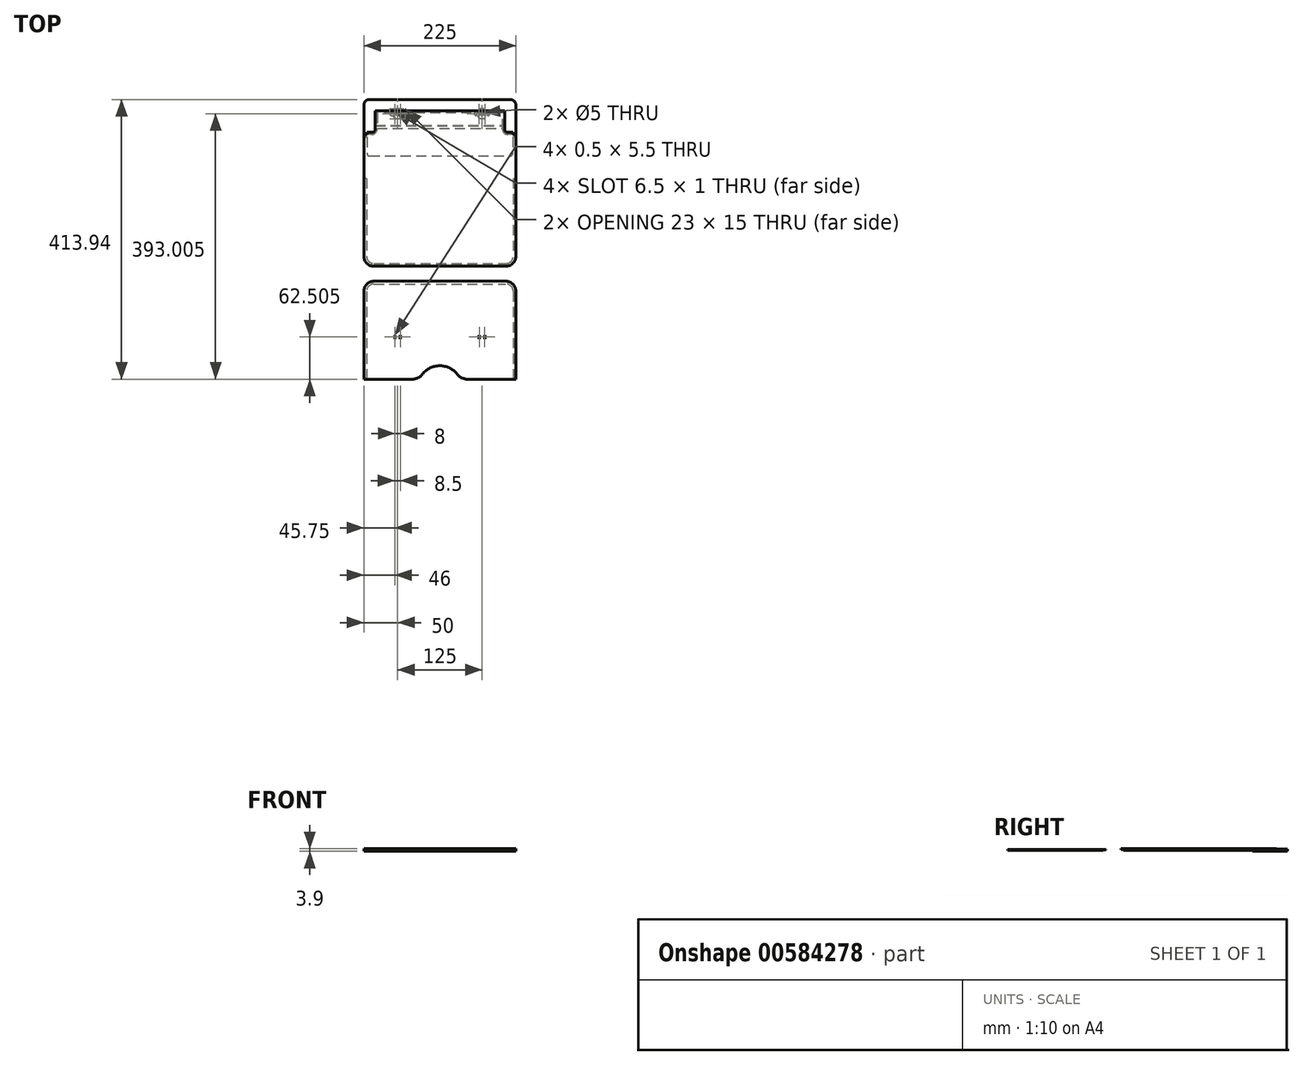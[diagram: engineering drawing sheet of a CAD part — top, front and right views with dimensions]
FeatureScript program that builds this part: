
annotation { "Feature Type Name" : "Feature", "Feature Type Description" : "" }
export const myFeature = defineFeature(function(context is Context, id is Id, definition is map)
    precondition{}
    {
        {
            var Q0;
            Q0=qCreatedBy(makeId("Top.planeOp"),FACE);
            var sketch = newSketch(context, id + "F0", { "sketchPlane" : qUnion([Q0])});
            skLineSegment(sketch, "E0.bottom", {"start": v(104.5, 206.97) * mm, "end": v(-104.5, 206.97) * mm});
            skLineSegment(sketch, "E0.top", {"start": v(-41.23, -206.97) * mm, "end": v(-112.5, -206.97) * mm});
            skLineSegment(sketch, "E0.left", {"start": v(112.5, 198.97) * mm, "end": v(112.5, 105.24) * mm});
            skLineSegment(sketch, "E0.right", {"start": v(-112.5, 198.97) * mm, "end": v(-112.5, 105.24) * mm});
            skPoint(sketch, "E0.middle", {"position": v(0, 0) * mm});
            skPoint(sketch, "E1", {"position": v(112.5, 123.54) * mm});
            skLineSegment(sketch, "E2", {"start": v(112.5, 155.4) * mm, "end": v(100.8, 155.4) * mm});
            skLineSegment(sketch, "E3", {"start": v(92.8, 163.4) * mm, "end": v(92.8, 187.27) * mm});
            skLineSegment(sketch, "E4", {"start": v(92.8, 187.27) * mm, "end": v(-92.8, 187.27) * mm});
            skLineSegment(sketch, "E5", {"start": v(-92.8, 187.27) * mm, "end": v(-92.8, 163.4) * mm});
            skLineSegment(sketch, "E6", {"start": v(-100.8, 155.4) * mm, "end": v(-112.5, 155.4) * mm});
            skLineSegment(sketch, "E7", {"start": v(-60.78, 187.27) * mm, "end": v(-60.78, 206.97) * mm, "construction": true});
            skPoint(sketch, "E8.visualSharp", {"position": v(-112.5, 206.97) * mm});
            skArc(sketch, "E8.filletArc", {"start": v(-104.5, 206.97) * mm, "mid": v(-110.16, 204.62) * mm, "end": v(-112.5, 198.97) * mm});
            skPoint(sketch, "E9.visualSharp", {"position": v(112.5, 206.97) * mm});
            skArc(sketch, "E9.filletArc", {"start": v(112.5, 198.97) * mm, "mid": v(110.16, 204.62) * mm, "end": v(104.5, 206.97) * mm});
            skPoint(sketch, "E10.visualSharp", {"position": v(92.8, 155.4) * mm});
            skArc(sketch, "E10.filletArc", {"start": v(92.8, 163.4) * mm, "mid": v(95.14, 157.74) * mm, "end": v(100.8, 155.4) * mm});
            skPoint(sketch, "E11.visualSharp", {"position": v(-92.8, 155.4) * mm});
            skArc(sketch, "E11.filletArc", {"start": v(-100.8, 155.4) * mm, "mid": v(-95.14, 157.74) * mm, "end": v(-92.8, 163.4) * mm});
            skLineSegment(sketch, "E12", {"start": v(-112.5, 145.44) * mm, "end": v(-92.8, 145.44) * mm, "construction": true});
            skLineSegment(sketch, "E13", {"start": v(112.5, 123.54) * mm, "end": v(-112.5, 123.54) * mm, "construction": true});
            skArc(sketch, "E14", {"start": v(25.52, -199.35) * mm, "mid": v(0, -186.97) * mm, "end": v(-25.52, -199.35) * mm});
            skPoint(sketch, "E15.newPointA", {"position": v(-30, -206.97) * mm});
            skPoint(sketch, "E15.newPointB", {"position": v(112.5, -206.97) * mm});
            skArc(sketch, "E15.filletArc", {"start": v(-41.23, -206.96) * mm, "mid": v(-32.5, -204.96) * mm, "end": v(-25.52, -199.35) * mm});
            skLineSegment(sketch, "E16", {"start": v(41.23, -206.97) * mm, "end": v(132.5, -206.96) * mm});
            skPoint(sketch, "E17.visualSharp", {"position": v(30, -206.97) * mm});
            skArc(sketch, "E17.filletArc", {"start": v(25.52, -199.35) * mm, "mid": v(32.5, -204.96) * mm, "end": v(41.23, -206.96) * mm});
            skLineSegment(sketch, "E18.0", {"start": v(-100.8, 158.4) * mm, "end": v(-108, 158.4) * mm});
            skArc(sketch, "E18.1", {"start": v(-100.8, 158.4) * mm, "mid": v(-97.26, 159.86) * mm, "end": v(-95.8, 163.4) * mm});
            skLineSegment(sketch, "E18.2", {"start": v(-95.8, 190.27) * mm, "end": v(-95.8, 163.4) * mm});
            skLineSegment(sketch, "E18.3", {"start": v(108, 158.4) * mm, "end": v(100.8, 158.4) * mm});
            skArc(sketch, "E18.4", {"start": v(95.8, 163.4) * mm, "mid": v(97.26, 159.86) * mm, "end": v(100.8, 158.4) * mm});
            skLineSegment(sketch, "E18.5", {"start": v(95.8, 163.4) * mm, "end": v(95.8, 190.27) * mm});
            skLineSegment(sketch, "E18.6", {"start": v(95.8, 190.27) * mm, "end": v(-95.8, 190.27) * mm});
            skLineSegment(sketch, "E19", {"start": v(-108, 158.4) * mm, "end": v(-108, 155.4) * mm});
            skLineSegment(sketch, "E20.MirrorCS", {"start": v(108, 158.4) * mm, "end": v(108, 155.4) * mm});
            skLineSegment(sketch, "E21", {"start": v(-97.5, -61.97) * mm, "end": v(97.5, -61.97) * mm});
            skLineSegment(sketch, "E22", {"start": v(-97.5, -39.77) * mm, "end": v(97.5, -39.77) * mm});
            skArc(sketch, "E23.filletArc", {"start": v(-112.5, -24.77) * mm, "mid": v(-108.1, -35.37) * mm, "end": v(-97.5, -39.77) * mm});
            skArc(sketch, "E24.filletArc", {"start": v(97.5, -39.77) * mm, "mid": v(108.1, -35.37) * mm, "end": v(112.5, -24.77) * mm});
            skLineSegment(sketch, "E25", {"start": v(-112.5, -76.97) * mm, "end": v(-112.5, -206.97) * mm});
            skLineSegment(sketch, "E26", {"start": v(112.5, -76.96) * mm, "end": v(112.5, -206.97) * mm});
            skPoint(sketch, "E27.visualSharp", {"position": v(-112.5, -61.97) * mm});
            skArc(sketch, "E27.filletArc", {"start": v(-97.5, -61.97) * mm, "mid": v(-108.1, -66.36) * mm, "end": v(-112.5, -76.97) * mm});
            skPoint(sketch, "E28.visualSharp", {"position": v(112.5, -61.97) * mm});
            skArc(sketch, "E28.filletArc", {"start": v(112.5, -76.96) * mm, "mid": v(108.1, -66.36) * mm, "end": v(97.5, -61.97) * mm});
            skLineSegment(sketch, "E29.bottom", {"start": v(-66.75, -141.72) * mm, "end": v(-66.25, -141.72) * mm});
            skLineSegment(sketch, "E29.top", {"start": v(-66.75, -147.22) * mm, "end": v(-66.25, -147.22) * mm});
            skLineSegment(sketch, "E29.left", {"start": v(-66.75, -141.72) * mm, "end": v(-66.75, -147.22) * mm});
            skLineSegment(sketch, "E29.right", {"start": v(-66.25, -141.72) * mm, "end": v(-66.25, -147.22) * mm});
            skLineSegment(sketch, "E30", {"start": v(-62.5, -148.65) * mm, "end": v(-62.5, -157.3) * mm, "construction": true});
            skPoint(sketch, "E31.orphan", {"position": v(-90.2, -187.28) * mm});
            skLineSegment(sketch, "E32.MirrorCS", {"start": v(-58.25, -147.22) * mm, "end": v(-58.75, -147.22) * mm});
            skLineSegment(sketch, "E33.MirrorCS", {"start": v(-58.75, -141.72) * mm, "end": v(-58.75, -147.22) * mm});
            skLineSegment(sketch, "E34.MirrorCS", {"start": v(-58.25, -141.72) * mm, "end": v(-58.25, -147.22) * mm});
            skLineSegment(sketch, "E35.MirrorCS", {"start": v(-58.25, -141.72) * mm, "end": v(-58.75, -141.72) * mm});
            skPoint(sketch, "E36", {"position": v(-62.5, -144.47) * mm});
            skLineSegment(sketch, "E37.trimOffspring", {"start": v(-66.25, -144.47) * mm, "end": v(-58.75, -144.47) * mm, "construction": true});
            skPoint(sketch, "E38.trimOffspring.end.orphan", {"position": v(-58.18, -144.47) * mm});
            skPoint(sketch, "E39.start.orphan", {"position": v(-66.82, -144.47) * mm});
            skLineSegment(sketch, "E40.MirrorCS", {"start": v(66.75, -147.22) * mm, "end": v(66.25, -147.22) * mm});
            skLineSegment(sketch, "E41.MirrorCS", {"start": v(66.75, -141.72) * mm, "end": v(66.25, -141.72) * mm});
            skLineSegment(sketch, "E42.MirrorCS", {"start": v(58.25, -141.72) * mm, "end": v(58.75, -141.72) * mm});
            skLineSegment(sketch, "E43.MirrorCS", {"start": v(58.25, -147.22) * mm, "end": v(58.75, -147.22) * mm});
            skPoint(sketch, "E44.MirrorP", {"position": v(66.82, -144.47) * mm});
            skLineSegment(sketch, "E45.MirrorCS", {"start": v(58.25, -141.72) * mm, "end": v(58.25, -147.21) * mm});
            skLineSegment(sketch, "E46.MirrorCS", {"start": v(66.25, -144.47) * mm, "end": v(58.75, -144.47) * mm, "construction": true});
            skLineSegment(sketch, "E47.MirrorCS", {"start": v(66.25, -141.72) * mm, "end": v(66.25, -147.21) * mm});
            skPoint(sketch, "E48.MirrorP", {"position": v(62.5, -144.47) * mm});
            skLineSegment(sketch, "E49.MirrorCS", {"start": v(66.75, -141.72) * mm, "end": v(66.75, -147.21) * mm});
            skLineSegment(sketch, "E50.MirrorCS", {"start": v(58.75, -141.72) * mm, "end": v(58.75, -147.21) * mm});
            skPoint(sketch, "E51.MirrorP", {"position": v(58.18, -144.47) * mm});
            skLineSegment(sketch, "E52", {"start": v(-112.5, 105.24) * mm, "end": v(112.5, 105.24) * mm, "construction": true});
            skLineSegment(sketch, "E53", {"start": v(-112.5, 105.24) * mm, "end": v(-112.5, -24.77) * mm});
            skLineSegment(sketch, "E54", {"start": v(112.5, 105.24) * mm, "end": v(112.5, -24.77) * mm});
            skSolve(sketch);
        }
        {
            var Q0;
            {var subQ1=sQuery(id+"F0.wireOp",EDGE,"E0.top");Q0=makeQuery(id+"F0.imprint","IMPRINT",FACE,{"disambiguationData":[TD([[makeQuery(id+"F0.imprint","IMPRINT",EDGE,{"derivedFrom":subQ1}),-1.0]])]});}
            extrude(context, id + "F1", {"entities" : qUnion([Q0]), "oppositeDirection" : true, "depth" : 0.8 * mm, "offsetDistance" : 25 * mm});
        }
        {
            var Q0;
            Q0=makeQuery(id+"F0.imprint","IMPRINT",FACE,{"disambiguationData":[TD([[makeQuery(id+"F0.imprint","IMPRINT",EDGE,{"derivedFrom":sQuery(id+"F0.wireOp",EDGE,"E3")}),1.0]])]});
            var Q1;
            Q1=makeQuery(id+"F0.imprint","IMPRINT",FACE,{"disambiguationData":[TD([[makeQuery(id+"F0.imprint","IMPRINT",EDGE,{"derivedFrom":sQuery(id+"F0.wireOp",EDGE,"E3")}),-1.0]])]});
            extrude(context, id + "F2", {"entities" : qUnion([Q0, Q1]), "depth" : 0.9 * mm, "offsetDistance" : 25 * mm});
        }
        {
            var Q0;
            Q0=makeQuery(id+"F0.imprint","IMPRINT",FACE,{"disambiguationData":[TD([[makeQuery(id+"F0.imprint","IMPRINT",EDGE,{"derivedFrom":sQuery(id+"F0.wireOp",EDGE,"E0.bottom")}),1.0]])]});
            extrude(context, id + "F3", {"entities" : qUnion([Q0]), "oppositeDirection" : true, "depth" : 0.9 * mm, "offsetDistance" : 25 * mm});
        }
        {
            var Q0;
            Q0=makeQuery(id+"F0.imprint","IMPRINT",FACE,{"disambiguationData":[TD([[makeQuery(id+"F0.imprint","IMPRINT",EDGE,{"derivedFrom":sQuery(id+"F0.wireOp",EDGE,"E3")}),-1.0]])]});
            var Q1;
            Q1=makeQuery(id+"F0.imprint","IMPRINT",FACE,{"disambiguationData":[TD([[makeQuery(id+"F0.imprint","IMPRINT",EDGE,{"derivedFrom":sQuery(id+"F0.wireOp",EDGE,"E0.bottom")}),1.0]])]});
            extrude(context, id + "F4", {"entities" : qUnion([Q0, Q1]), "depth" : 0.6 * mm, "offsetDistance" : 25 * mm});
        }
        {
            var Q0;
            Q0=makeQuery(id+"F3.opExtrude","CAP_FACE",FACE,{"disambiguationData":[OSD([sQuery(id+"F0.wireOp",EDGE,"E0.bottom"),sQuery(id+"F0.wireOp",EDGE,"E0.left"),sQuery(id+"F0.wireOp",EDGE,"E0.right"),sQuery(id+"F0.wireOp",EDGE,"E2"),sQuery(id+"F0.wireOp",EDGE,"E6"),sQuery(id+"F0.wireOp",EDGE,"E8.filletArc"),sQuery(id+"F0.wireOp",EDGE,"E9.filletArc"),sQuery(id+"F0.wireOp",EDGE,"E18.0"),sQuery(id+"F0.wireOp",EDGE,"E18.2"),sQuery(id+"F0.wireOp",EDGE,"E18.3"),sQuery(id+"F0.wireOp",EDGE,"E18.5"),sQuery(id+"F0.wireOp",EDGE,"E18.6"),sQuery(id+"F0.wireOp",EDGE,"E19"),sQuery(id+"F0.wireOp",EDGE,"E20.MirrorCS")])],"isStart":false});
            var sketch = newSketch(context, id + "F5", { "sketchPlane" : qUnion([Q0])});
            skLineSegment(sketch, "E55.0", {"start": v(-112.5, -198.97) * mm, "end": v(-112.5, -155.4) * mm});
            skArc(sketch, "E56.0", {"start": v(-104.5, -206.97) * mm, "mid": v(-110.16, -204.62) * mm, "end": v(-112.5, -198.97) * mm});
            skLineSegment(sketch, "E57.0", {"start": v(104.5, -206.97) * mm, "end": v(-104.5, -206.97) * mm});
            skArc(sketch, "E58.0", {"start": v(112.5, -198.97) * mm, "mid": v(110.16, -204.62) * mm, "end": v(104.5, -206.97) * mm});
            skLineSegment(sketch, "E59.0", {"start": v(112.5, -198.97) * mm, "end": v(112.5, -155.4) * mm});
            skPoint(sketch, "E60.orphan", {"position": v(-112.5, -105.24) * mm});
            skPoint(sketch, "E61.orphan", {"position": v(112.5, -105.24) * mm});
            skLineSegment(sketch, "E62", {"start": v(-108, -151.26) * mm, "end": v(-108, -127.54) * mm});
            skArc(sketch, "E63", {"start": v(-108.36, -151.66) * mm, "mid": v(-110.78, -152.87) * mm, "end": v(-111.75, -155.4) * mm});
            skArc(sketch, "E64.filletArc", {"start": v(-108.36, -151.66) * mm, "mid": v(-108.1, -151.53) * mm, "end": v(-108, -151.26) * mm});
            skLineSegment(sketch, "E65.0", {"start": v(0, -123.54) * mm, "end": v(-104, -123.54) * mm});
            skPoint(sketch, "E66.newPointB", {"position": v(-112.5, -123.54) * mm});
            skArc(sketch, "E66.filletArc", {"start": v(-104, -123.54) * mm, "mid": v(-106.83, -124.7) * mm, "end": v(-108, -127.54) * mm});
            skPoint(sketch, "E67.orphan", {"position": v(112.5, -123.54) * mm});
            skLineSegment(sketch, "E68.MirrorCS", {"start": v(0, -123.54) * mm, "end": v(104, -123.54) * mm});
            skArc(sketch, "E69.MirrorCS", {"start": v(104, -123.54) * mm, "mid": v(106.83, -124.7) * mm, "end": v(108, -127.54) * mm});
            skLineSegment(sketch, "E70.MirrorCS", {"start": v(108, -151.26) * mm, "end": v(108, -127.54) * mm});
            skArc(sketch, "E71.MirrorCS", {"start": v(108.36, -151.66) * mm, "mid": v(108.1, -151.53) * mm, "end": v(108, -151.26) * mm});
            skArc(sketch, "E72.MirrorCS", {"start": v(108.36, -151.66) * mm, "mid": v(110.78, -152.87) * mm, "end": v(111.75, -155.4) * mm});
            skLineSegment(sketch, "E73", {"start": v(-112.5, -155.4) * mm, "end": v(-111.75, -155.4) * mm});
            skLineSegment(sketch, "E74", {"start": v(111.75, -155.4) * mm, "end": v(112.5, -155.4) * mm});
            skSolve(sketch);
        }
        {
            var Q0;
            Q0=qSketchRegion(id+"F5",true);
            extrude(context, id + "F6", {"entities" : qUnion([Q0]), "depth" : 0.6 * mm, "offsetDistance" : 25 * mm});
        }
        {
            var Q0;
            Q0=makeQuery(id+"F6.opExtrude","CAP_FACE",FACE,{"disambiguationData":[OSD([sQuery(id+"F5.wireOp",EDGE,"E55.0"),sQuery(id+"F5.wireOp",EDGE,"E56.0"),sQuery(id+"F5.wireOp",EDGE,"E57.0"),sQuery(id+"F5.wireOp",EDGE,"E58.0"),sQuery(id+"F5.wireOp",EDGE,"E59.0"),sQuery(id+"F5.wireOp",EDGE,"mqd3fcgL-vkYM-jt8C-SEZb-QTAqxbzKtnkH"),sQuery(id+"F5.wireOp",EDGE,"E62"),sQuery(id+"F5.wireOp",EDGE,"E63"),sQuery(id+"F5.wireOp",EDGE,"030e1fa7-f3c1-437d-8277-750ec2e293a4.filletArc"),sQuery(id+"F5.wireOp",EDGE,"E64.filletArc"),sQuery(id+"F5.wireOp",EDGE,"E65.0"),sQuery(id+"F5.wireOp",EDGE,"E66.filletArc"),sQuery(id+"F5.wireOp",EDGE,"E68.MirrorCS"),sQuery(id+"F5.wireOp",EDGE,"E69.MirrorCS"),sQuery(id+"F5.wireOp",EDGE,"E70.MirrorCS"),sQuery(id+"F5.wireOp",EDGE,"E71.MirrorCS"),sQuery(id+"F5.wireOp",EDGE,"E72.MirrorCS"),sQuery(id+"F5.wireOp",EDGE,"eea31a7d-e614-436a-bde2-b2130c57034b0.MirrorCS"),sQuery(id+"F5.wireOp",EDGE,"bd1179cf-cb36-4206-b0af-3bf9bbb72a3d0.MirrorCS")])],"isStart":false});
            var sketch = newSketch(context, id + "F7", { "sketchPlane" : qUnion([Q0])});
            skLineSegment(sketch, "E75.0.0", {"start": v(-108, -155.4) * mm, "end": v(-108, -158.4) * mm});
            skLineSegment(sketch, "E75.0.1", {"start": v(-108, -158.4) * mm, "end": v(-100.8, -158.4) * mm});
            skArc(sketch, "E75.0.2", {"start": v(-100.8, -158.4) * mm, "mid": v(-97.26, -159.86) * mm, "end": v(-95.8, -163.4) * mm});
            skLineSegment(sketch, "E75.0.3", {"start": v(-95.8, -163.4) * mm, "end": v(-95.8, -168.4) * mm});
            skLineSegment(sketch, "E75.0.5", {"start": v(95.8, -168.4) * mm, "end": v(95.8, -163.4) * mm});
            skArc(sketch, "E75.0.6", {"start": v(95.8, -163.4) * mm, "mid": v(97.26, -159.86) * mm, "end": v(100.8, -158.4) * mm});
            skLineSegment(sketch, "E75.0.7", {"start": v(100.8, -158.4) * mm, "end": v(108, -158.4) * mm});
            skLineSegment(sketch, "E75.0.8", {"start": v(108, -158.4) * mm, "end": v(108, -155.4) * mm});
            skLineSegment(sketch, "E75.0.9", {"start": v(108, -155.4) * mm, "end": v(112.5, -155.4) * mm});
            skLineSegment(sketch, "E75.0.10", {"start": v(112.5, -155.4) * mm, "end": v(112.5, -198.97) * mm});
            skArc(sketch, "E75.0.11", {"start": v(112.5, -198.97) * mm, "mid": v(110.16, -204.62) * mm, "end": v(104.5, -206.96) * mm});
            skLineSegment(sketch, "E75.0.12", {"start": v(104.5, -206.97) * mm, "end": v(-104.5, -206.97) * mm});
            skArc(sketch, "E75.0.13", {"start": v(-104.5, -206.97) * mm, "mid": v(-110.16, -204.62) * mm, "end": v(-112.5, -198.97) * mm});
            skLineSegment(sketch, "E75.0.14", {"start": v(-112.5, -198.97) * mm, "end": v(-112.5, -155.4) * mm});
            skLineSegment(sketch, "E75.0.15", {"start": v(-112.5, -155.4) * mm, "end": v(-108, -155.4) * mm});
            skLineSegment(sketch, "E76", {"start": v(-95.8, -168.4) * mm, "end": v(95.8, -168.4) * mm});
            skPoint(sketch, "E75.0.4.end.orphan", {"position": v(95.8, -190.27) * mm});
            skPoint(sketch, "E75.0.4.start.orphan", {"position": v(-95.8, -190.27) * mm});
            skArc(sketch, "E77", {"start": v(-69.57, -188.54) * mm, "mid": v(-62.5, -193.54) * mm, "end": v(-55.43, -188.54) * mm});
            skLineSegment(sketch, "E78", {"start": v(-71.5, -186.04) * mm, "end": v(-53.5, -186.04) * mm, "construction": true});
            skLineSegment(sketch, "E79", {"start": v(-62.5, -233.39) * mm, "end": v(-62.5, -178.54) * mm, "construction": true});
            skArc(sketch, "E80.0.startCap", {"start": v(-71.5, -188.54) * mm, "mid": v(-74, -186.04) * mm, "end": v(-71.5, -183.54) * mm});
            skArc(sketch, "E80.0.endCap", {"start": v(-53.5, -183.54) * mm, "mid": v(-51, -186.04) * mm, "end": v(-53.5, -188.54) * mm});
            skLineSegment(sketch, "E80.0.left", {"start": v(-71.5, -183.54) * mm, "end": v(-69.57, -183.54) * mm});
            skLineSegment(sketch, "E80.0.right", {"start": v(-71.5, -188.54) * mm, "end": v(-69.57, -188.54) * mm});
            skLineSegment(sketch, "E81.trimOffspring", {"start": v(-55.43, -183.54) * mm, "end": v(-53.5, -183.54) * mm});
            skLineSegment(sketch, "E82.trimOffspring", {"start": v(-55.43, -188.54) * mm, "end": v(-53.5, -188.54) * mm});
            skArc(sketch, "E83.trimOffspring", {"start": v(-55.43, -183.53) * mm, "mid": v(-62.5, -178.54) * mm, "end": v(-69.57, -183.53) * mm});
            skArc(sketch, "E84.MirrorCS", {"start": v(69.57, -188.54) * mm, "mid": v(62.5, -193.54) * mm, "end": v(55.43, -188.54) * mm});
            skLineSegment(sketch, "E85.MirrorCS", {"start": v(71.5, -188.54) * mm, "end": v(69.57, -188.54) * mm});
            skArc(sketch, "E86.MirrorCS", {"start": v(71.5, -188.54) * mm, "mid": v(74, -186.04) * mm, "end": v(71.5, -183.54) * mm});
            skLineSegment(sketch, "E87.MirrorCS", {"start": v(71.5, -183.54) * mm, "end": v(69.57, -183.54) * mm});
            skArc(sketch, "E88.MirrorCS", {"start": v(55.43, -183.53) * mm, "mid": v(62.5, -178.54) * mm, "end": v(69.57, -183.53) * mm});
            skLineSegment(sketch, "E89.MirrorCS", {"start": v(55.43, -183.54) * mm, "end": v(53.5, -183.54) * mm});
            skArc(sketch, "E90.MirrorCS", {"start": v(53.5, -183.54) * mm, "mid": v(51, -186.04) * mm, "end": v(53.5, -188.54) * mm});
            skLineSegment(sketch, "E91.MirrorCS", {"start": v(55.43, -188.54) * mm, "end": v(53.5, -188.54) * mm});
            skSolve(sketch);
        }
        {
            var Q0;
            {var subQ1=sQuery(id+"F7.wireOp",EDGE,"E75.0.0");Q0=makeQuery(id+"F7.imprint","IMPRINT",FACE,{"disambiguationData":[TD([[makeQuery(id+"F7.imprint","IMPRINT",EDGE,{"derivedFrom":subQ1}),-1.0]])]});}
            extrude(context, id + "F8", {"entities" : qUnion([Q0]), "depth" : 0.9 * mm, "offsetDistance" : 25 * mm});
        }
        {
            var Q0;
            Q0=makeQuery(id+"F8.opExtrude","CAP_FACE",FACE,{"disambiguationData":[OSD([sQuery(id+"F5.wireOp",EDGE,"mqd3fcgL-vkYM-jt8C-SEZb-QTAqxbzKtnkH"),sQuery(id+"F5.wireOp",EDGE,"030e1fa7-f3c1-437d-8277-750ec2e293a4.filletArc"),sQuery(id+"F5.wireOp",EDGE,"eea31a7d-e614-436a-bde2-b2130c57034b0.MirrorCS"),sQuery(id+"F5.wireOp",EDGE,"bd1179cf-cb36-4206-b0af-3bf9bbb72a3d0.MirrorCS"),sQuery(id+"F7.wireOp",EDGE,"E75.0.0"),sQuery(id+"F7.wireOp",EDGE,"E75.0.1"),sQuery(id+"F7.wireOp",EDGE,"E75.0.2"),sQuery(id+"F7.wireOp",EDGE,"E75.0.3"),sQuery(id+"F7.wireOp",EDGE,"E75.0.5"),sQuery(id+"F7.wireOp",EDGE,"E75.0.6"),sQuery(id+"F7.wireOp",EDGE,"E75.0.7"),sQuery(id+"F7.wireOp",EDGE,"E75.0.8"),sQuery(id+"F7.wireOp",EDGE,"E75.0.9"),sQuery(id+"F7.wireOp",EDGE,"E75.0.10"),sQuery(id+"F7.wireOp",EDGE,"E75.0.11"),sQuery(id+"F7.wireOp",EDGE,"E75.0.12"),sQuery(id+"F7.wireOp",EDGE,"E75.0.13"),sQuery(id+"F7.wireOp",EDGE,"E75.0.14"),sQuery(id+"F7.wireOp",EDGE,"E75.0.15"),sQuery(id+"F7.wireOp",EDGE,"E76"),sQuery(id+"F7.wireOp",EDGE,"E77"),sQuery(id+"F7.wireOp",EDGE,"E80.0.startCap"),sQuery(id+"F7.wireOp",EDGE,"E80.0.endCap"),sQuery(id+"F7.wireOp",EDGE,"E80.0.left"),sQuery(id+"F7.wireOp",EDGE,"E80.0.right"),sQuery(id+"F7.wireOp",EDGE,"E81.trimOffspring"),sQuery(id+"F7.wireOp",EDGE,"E82.trimOffspring"),sQuery(id+"F7.wireOp",EDGE,"E83.trimOffspring"),sQuery(id+"F7.wireOp",EDGE,"E84.MirrorCS"),sQuery(id+"F7.wireOp",EDGE,"E85.MirrorCS"),sQuery(id+"F7.wireOp",EDGE,"E86.MirrorCS"),sQuery(id+"F7.wireOp",EDGE,"E87.MirrorCS"),sQuery(id+"F7.wireOp",EDGE,"E88.MirrorCS"),sQuery(id+"F7.wireOp",EDGE,"E89.MirrorCS"),sQuery(id+"F7.wireOp",EDGE,"E90.MirrorCS"),sQuery(id+"F7.wireOp",EDGE,"E91.MirrorCS")])],"isStart":false});
            var sketch = newSketch(context, id + "F9", { "sketchPlane" : qUnion([Q0])});
            skLineSegment(sketch, "E92.0.0", {"start": v(-112.5, -198.97) * mm, "end": v(-112.5, -155.4) * mm});
            skLineSegment(sketch, "E92.0.1", {"start": v(-112.5, -155.4) * mm, "end": v(-100.8, -155.4) * mm});
            skArc(sketch, "E92.0.2", {"start": v(-100.8, -155.4) * mm, "mid": v(-95.14, -157.74) * mm, "end": v(-92.8, -163.4) * mm});
            skArc(sketch, "E92.0.6", {"start": v(92.8, -163.4) * mm, "mid": v(95.14, -157.74) * mm, "end": v(100.8, -155.4) * mm});
            skLineSegment(sketch, "E92.0.7", {"start": v(100.8, -155.4) * mm, "end": v(112.5, -155.4) * mm});
            skLineSegment(sketch, "E92.0.8", {"start": v(112.5, -155.4) * mm, "end": v(112.5, -198.97) * mm});
            skArc(sketch, "E92.0.9", {"start": v(112.5, -198.97) * mm, "mid": v(110.16, -204.62) * mm, "end": v(104.5, -206.96) * mm});
            skLineSegment(sketch, "E92.0.10", {"start": v(104.5, -206.97) * mm, "end": v(-104.5, -206.97) * mm});
            skArc(sketch, "E92.0.11", {"start": v(-104.5, -206.97) * mm, "mid": v(-110.16, -204.62) * mm, "end": v(-112.5, -198.97) * mm});
            skPoint(sketch, "E93.startSnap0", {"position": v(-110.7, -160.97) * mm});
            skPoint(sketch, "E92.0.4.end.orphan", {"position": v(92.8, -187.27) * mm});
            skPoint(sketch, "E92.0.4.start.orphan", {"position": v(-92.8, -187.27) * mm});
            skArc(sketch, "E94.0", {"start": v(-55.43, -183.53) * mm, "mid": v(-62.5, -178.54) * mm, "end": v(-69.57, -183.54) * mm, "construction": true});
            skCircle(sketch, "E95", {"center": v(-62.5, -186.04) * mm, "radius": 2.5 * mm});
            skLineSegment(sketch, "E96.left", {"start": v(-67.25, -183.28) * mm, "end": v(-67.25, -188.79) * mm});
            skLineSegment(sketch, "E96.right", {"start": v(-66.25, -183.29) * mm, "end": v(-66.25, -188.79) * mm});
            skLineSegment(sketch, "E97", {"start": v(-62.5, -193.54) * mm, "end": v(-62.5, -186.04) * mm, "construction": true});
            skLineSegment(sketch, "E98.MirrorCS", {"start": v(-57.75, -183.28) * mm, "end": v(-57.75, -188.79) * mm});
            skLineSegment(sketch, "E99.MirrorCS", {"start": v(-58.75, -183.29) * mm, "end": v(-58.75, -188.79) * mm});
            skLineSegment(sketch, "E100", {"start": v(-65, -186.04) * mm, "end": v(-60, -186.04) * mm, "construction": true});
            skLineSegment(sketch, "E101", {"start": v(-92.8, -163.4) * mm, "end": v(-92.8, -164.4) * mm});
            skLineSegment(sketch, "E102", {"start": v(-92.8, -164.4) * mm, "end": v(92.8, -164.4) * mm});
            skLineSegment(sketch, "E103", {"start": v(92.8, -164.4) * mm, "end": v(92.8, -163.4) * mm});
            skArc(sketch, "E104", {"start": v(-66.25, -183.29) * mm, "mid": v(-66.75, -182.79) * mm, "end": v(-67.25, -183.29) * mm});
            skArc(sketch, "E105.MirrorCS", {"start": v(-66.25, -188.79) * mm, "mid": v(-66.75, -189.29) * mm, "end": v(-67.25, -188.79) * mm});
            skArc(sketch, "E106.MirrorCS", {"start": v(-58.75, -188.79) * mm, "mid": v(-58.25, -189.29) * mm, "end": v(-57.75, -188.79) * mm});
            skArc(sketch, "E107.MirrorCS", {"start": v(-58.75, -183.29) * mm, "mid": v(-58.25, -182.79) * mm, "end": v(-57.75, -183.29) * mm});
            skLineSegment(sketch, "E108.MirrorCS", {"start": v(67.25, -183.28) * mm, "end": v(67.25, -188.79) * mm});
            skArc(sketch, "E109.MirrorCS", {"start": v(58.75, -188.79) * mm, "mid": v(58.25, -189.29) * mm, "end": v(57.75, -188.79) * mm});
            skArc(sketch, "E110.MirrorCS", {"start": v(66.25, -188.79) * mm, "mid": v(66.75, -189.29) * mm, "end": v(67.25, -188.79) * mm});
            skLineSegment(sketch, "E111.MirrorCS", {"start": v(58.75, -183.29) * mm, "end": v(58.75, -188.79) * mm});
            skCircle(sketch, "E112.MirrorC", {"center": v(62.5, -186.04) * mm, "radius": 2.5 * mm});
            skLineSegment(sketch, "E113.MirrorCS", {"start": v(57.75, -183.28) * mm, "end": v(57.75, -188.79) * mm});
            skArc(sketch, "E114.MirrorCS", {"start": v(66.25, -183.29) * mm, "mid": v(66.75, -182.79) * mm, "end": v(67.25, -183.29) * mm});
            skArc(sketch, "E115.MirrorCS", {"start": v(58.75, -183.29) * mm, "mid": v(58.25, -182.79) * mm, "end": v(57.75, -183.29) * mm});
            skLineSegment(sketch, "E116.MirrorCS", {"start": v(66.25, -183.29) * mm, "end": v(66.25, -188.79) * mm});
            skLineSegment(sketch, "E117.MirrorCS", {"start": v(65, -186.04) * mm, "end": v(60, -186.04) * mm, "construction": true});
            skSolve(sketch);
        }
        {
            var Q0;
            Q0=qSketchRegion(id+"F9",true);
            extrude(context, id + "F10", {"entities" : qUnion([Q0]), "depth" : 0.6 * mm, "offsetDistance" : 25 * mm});
        }
        {
            var Q0;
            Q0=makeQuery(id+"F1.opExtrude","CAP_FACE",FACE,{"disambiguationData":[OSD([sQuery(id+"F0.wireOp",EDGE,"E0.top"),sQuery(id+"F0.wireOp",EDGE,"E0.left"),sQuery(id+"F0.wireOp",EDGE,"E0.right"),sQuery(id+"F0.wireOp",EDGE,"E14"),sQuery(id+"F0.wireOp",EDGE,"E15.filletArc"),sQuery(id+"F0.wireOp",EDGE,"E16"),sQuery(id+"F0.wireOp",EDGE,"E17.filletArc"),sQuery(id+"F0.wireOp",EDGE,"E21")])],"isStart":false});
            var sketch = newSketch(context, id + "F11", { "sketchPlane" : qUnion([Q0])});
            skLineSegment(sketch, "E118.0.2", {"start": v(108.5, 206.96) * mm, "end": v(41.23, 206.97) * mm});
            skArc(sketch, "E118.0.3", {"start": v(41.23, 206.97) * mm, "mid": v(32.5, 204.96) * mm, "end": v(25.52, 199.35) * mm});
            skArc(sketch, "E118.0.4", {"start": v(25.52, 199.35) * mm, "mid": v(0, 186.97) * mm, "end": v(-25.52, 199.35) * mm});
            skArc(sketch, "E118.0.5", {"start": v(-25.52, 199.35) * mm, "mid": v(-32.5, 204.96) * mm, "end": v(-41.23, 206.96) * mm});
            skLineSegment(sketch, "E118.0.6", {"start": v(-41.23, 206.97) * mm, "end": v(-108.5, 206.97) * mm});
            skLineSegment(sketch, "E119.0.0", {"start": v(112.5, -155.4) * mm, "end": v(108, -155.4) * mm});
            skLineSegment(sketch, "E119.0.1", {"start": v(108, -155.4) * mm, "end": v(108, -158.4) * mm});
            skLineSegment(sketch, "E119.0.2", {"start": v(108, -158.4) * mm, "end": v(100.8, -158.4) * mm});
            skArc(sketch, "E119.0.3", {"start": v(100.8, -158.4) * mm, "mid": v(97.26, -159.86) * mm, "end": v(95.8, -163.4) * mm});
            skLineSegment(sketch, "E119.0.4", {"start": v(95.8, -163.4) * mm, "end": v(95.8, -168.97) * mm});
            skArc(sketch, "E119.0.7", {"start": v(-95.8, -163.4) * mm, "mid": v(-97.26, -159.86) * mm, "end": v(-100.8, -158.4) * mm});
            skLineSegment(sketch, "E119.0.8", {"start": v(-100.8, -158.4) * mm, "end": v(-108, -158.4) * mm});
            skLineSegment(sketch, "E119.0.9", {"start": v(-108, -158.4) * mm, "end": v(-108, -155.4) * mm});
            skLineSegment(sketch, "E119.0.10", {"start": v(-108, -155.4) * mm, "end": v(-112.5, -155.4) * mm});
            skLineSegment(sketch, "E119.0.11", {"start": v(-112.5, -155.4) * mm, "end": v(-112.5, -90.23) * mm});
            skLineSegment(sketch, "E119.0.13", {"start": v(112.5, -90.23) * mm, "end": v(112.5, -155.4) * mm});
            skLineSegment(sketch, "E120", {"start": v(-108.5, -90.24) * mm, "end": v(-112.5, -90.24) * mm});
            skLineSegment(sketch, "E121.MirrorCS", {"start": v(108.5, -90.24) * mm, "end": v(112.5, -90.24) * mm});
            skPoint(sketch, "E118.0.7.start.orphan", {"position": v(-41.23, 206.97) * mm});
            skPoint(sketch, "E118.0.1.end.orphan", {"position": v(132.5, 206.96) * mm});
            skPoint(sketch, "E122.orphan", {"position": v(-97.5, 61.97) * mm});
            skPoint(sketch, "E123.orphan", {"position": v(97.5, 39.77) * mm});
            skLineSegment(sketch, "E124.0", {"start": v(108.5, -236.93) * mm, "end": v(108.5, -158.4) * mm});
            skLineSegment(sketch, "E124.1", {"start": v(-108.5, -90.24) * mm, "end": v(-108.5, 24.77) * mm});
            skArc(sketch, "E124.2", {"start": v(-108.5, 24.77) * mm, "mid": v(-105.28, 32.54) * mm, "end": v(-97.5, 35.77) * mm});
            skLineSegment(sketch, "E124.3", {"start": v(-97.5, 35.77) * mm, "end": v(97.5, 35.77) * mm});
            skArc(sketch, "E124.4", {"start": v(97.5, 35.77) * mm, "mid": v(105.28, 32.54) * mm, "end": v(108.5, 24.77) * mm});
            skLineSegment(sketch, "E125.trimOffspring", {"start": v(108.5, -90.24) * mm, "end": v(108.5, 24.77) * mm});
            skPoint(sketch, "E126.orphan", {"position": v(-112.5, -155.4) * mm});
            skLineSegment(sketch, "E127.0", {"start": v(-108.5, 76.97) * mm, "end": v(-108.5, 206.97) * mm});
            skLineSegment(sketch, "E127.1", {"start": v(108.5, 76.96) * mm, "end": v(108.5, 206.97) * mm});
            skArc(sketch, "E127.2", {"start": v(108.5, 76.96) * mm, "mid": v(105.28, 69.19) * mm, "end": v(97.5, 65.97) * mm});
            skLineSegment(sketch, "E127.3", {"start": v(-97.5, 65.97) * mm, "end": v(97.5, 65.97) * mm});
            skArc(sketch, "E127.4", {"start": v(-97.5, 65.97) * mm, "mid": v(-105.28, 69.19) * mm, "end": v(-108.5, 76.97) * mm});
            skPoint(sketch, "E128.orphan", {"position": v(122.59, -205.03) * mm});
            skPoint(sketch, "E129.orphan", {"position": v(-92.8, -205.03) * mm});
            skPoint(sketch, "E119.0.5.end.orphan", {"position": v(-95.8, -190.27) * mm});
            skPoint(sketch, "E130.orphan", {"position": v(95.8, -190.27) * mm});
            skLineSegment(sketch, "E131.0", {"start": v(-95.8, -168.97) * mm, "end": v(95.8, -168.97) * mm});
            skPoint(sketch, "E132.orphan", {"position": v(-92.8, -168.97) * mm});
            skPoint(sketch, "E133.orphan", {"position": v(92.8, -168.97) * mm});
            skLineSegment(sketch, "E134.trimOffspring", {"start": v(-95.8, -168.97) * mm, "end": v(-95.8, -163.4) * mm});
            skSolve(sketch);
        }
        {
            var Q0;
            Q0=qSketchRegion(id+"F11",true);
            extrude(context, id + "F12", {"entities" : qUnion([Q0]), "depth" : 0.6 * mm, "offsetDistance" : 25 * mm});
        }
    });
